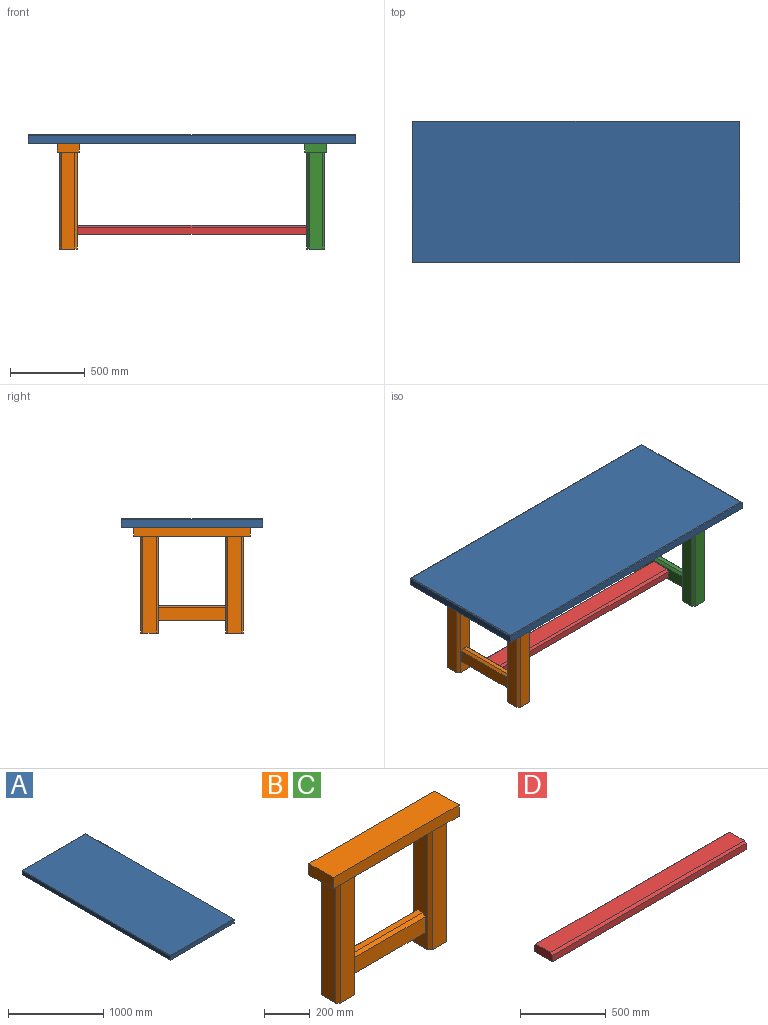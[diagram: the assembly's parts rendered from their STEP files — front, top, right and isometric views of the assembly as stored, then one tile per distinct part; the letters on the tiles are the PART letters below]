
ASSEMBLY  parts=4 mates=4
PART A: 10 faces, bbox 950x2200x55 mm
  f0: plane 950x50mm, normal (0,1,0), area 47500mm2, adj f1,f3,f4,f6
  f1: plane 2200x50mm, normal (-1,0,0), area 110000mm2, adj f0,f2,f4,f7
  f2: plane 950x50mm, normal (0,-1,0), area 47500mm2, adj f1,f3,f4,f9
  f3: plane 2200x50mm, normal (1,0,0), area 110000mm2, adj f0,f2,f4,f8
  f4: plane 2200x950mm, normal (0,0,-1), area 2090000mm2, adj f0,f1,f2,f3
  f5: plane 2190x940mm, normal (0,0,1), area 2058600mm2, adj f6,f7,f8,f9
  f6: cylinder r=5mm len=950mm, axis (-1,0,0), area 7432.7mm2, adj f0,f5,f7,f8
  f7: cylinder r=5mm len=2200mm, axis (0,-1,0), area 17250.2mm2, adj f1,f5,f6,f9
  f8: cylinder r=5mm len=2200mm, axis (0,1,0), area 17250.2mm2, adj f3,f5,f6,f9
  f9: cylinder r=5mm len=950mm, axis (1,0,0), area 7432.7mm2, adj f2,f5,f7,f8
PART B: 30 faces, bbox 780x150x710 mm
  f0: plane 150x60mm, normal (-1,0,0), area 9000mm2, adj f1,f3,f4,f5
  f1: plane 780x60mm, normal (0,-1,0), area 46800mm2, adj f0,f2,f4,f5
  f2: plane 150x60mm, normal (1,0,0), area 9000mm2, adj f1,f3,f4,f5
  f3: plane 780x60mm, normal (0,1,0), area 46800mm2, adj f0,f2,f4,f5
  f4: plane 780x150mm, normal (0,0,1), area 117000mm2, adj f0,f1,f2,f3
  f5: plane 780x150mm, normal (0,0,-1), area 89100mm2, adj f0,f1,f2,f3,f6,f7,f8,f9
  f6: plane 650x90mm, normal (0,-1,0), area 58500mm2, adj f5,f10,f17,f22
  f7: plane 650x90mm, normal (-1,0,0), area 52725mm2, adj f5,f10,f22,f23,f24,f25,f26,f27
  f8: plane 650x90mm, normal (0,1,0), area 58500mm2, adj f5,f10,f16,f23
  f9: plane 650x90mm, normal (1,0,0), area 58500mm2, adj f5,f10,f16,f17
  f10: plane 120x120mm, normal (0,0,-1), area 13950mm2, adj f6,f7,f8,f9,f16,f17,f22,f23
  f11: plane 650x90mm, normal (0,-1,0), area 58500mm2, adj f5,f15,f18,f19
  f12: plane 650x90mm, normal (-1,0,0), area 58500mm2, adj f5,f15,f19,f20
  f13: plane 650x90mm, normal (0,1,0), area 58500mm2, adj f5,f15,f20,f21
  f14: plane 650x90mm, normal (1,0,0), area 52725mm2, adj f5,f15,f18,f21,f24,f25,f26,f27
  f15: plane 120x120mm, normal (0,0,-1), area 13950mm2, adj f11,f12,f13,f14,f18,f19,f20,f21
  f16: plane 650x15mm, normal (0.71,0.71,0), area 13788.6mm2, adj f5,f8,f9,f10
  f17: plane 650x15mm, normal (0.71,-0.71,0), area 13788.6mm2, adj f5,f6,f9,f10
  f18: plane 650x15mm, normal (0.71,-0.71,0), area 13788.6mm2, adj f5,f11,f14,f15
  f19: plane 650x15mm, normal (-0.71,-0.71,0), area 13788.6mm2, adj f5,f11,f12,f15
  f20: plane 650x15mm, normal (-0.71,0.71,0), area 13788.6mm2, adj f5,f12,f13,f15
  f21: plane 650x15mm, normal (0.71,0.71,0), area 13788.6mm2, adj f5,f13,f14,f15
  f22: plane 650x15mm, normal (-0.71,-0.71,0), area 13788.6mm2, adj f5,f6,f7,f10
  f23: plane 650x15mm, normal (-0.71,0.71,0), area 13788.6mm2, adj f5,f7,f8,f10
  f24: plane 450x30mm, normal (0,0,1), area 13500mm2, adj f7,f14,f28,f29
  f25: plane 450x85mm, normal (0,1,0), area 38250mm2, adj f7,f14,f26,f29
  f26: plane 450x60mm, normal (0,0,-1), area 27000mm2, adj f7,f14,f25,f27
  f27: plane 450x85mm, normal (0,-1,0), area 38250mm2, adj f7,f14,f26,f28
  f28: plane 450x15mm, normal (0,-0.71,0.71), area 9545.9mm2, adj f7,f14,f24,f27
  f29: plane 450x15mm, normal (0,0.71,0.71), area 9545.9mm2, adj f7,f14,f24,f25
PART C: same geometry as B
PART D: 8 faces, bbox 1600x150x60 mm
  f0: plane 150x60mm, normal (-1,0,0), area 8775mm2, adj f1,f3,f4,f5,f6,f7
  f1: plane 1600x45mm, normal (0,-1,0), area 72000mm2, adj f0,f2,f5,f7
  f2: plane 150x60mm, normal (1,0,0), area 8775mm2, adj f1,f3,f4,f5,f6,f7
  f3: plane 1600x45mm, normal (0,1,0), area 72000mm2, adj f0,f2,f5,f6
  f4: plane 1600x120mm, normal (0,0,1), area 192000mm2, adj f0,f2,f6,f7
  f5: plane 1600x150mm, normal (0,0,-1), area 240000mm2, adj f0,f1,f2,f3
  f6: plane 1600x15mm, normal (0,0.71,0.71), area 33941.1mm2, adj f0,f2,f3,f4
  f7: plane 1600x15mm, normal (0,-0.71,0.71), area 33941.1mm2, adj f0,f1,f2,f4
PLACE A rot(axis=(0,0,1),90deg) t=(2877.51,-730.43,-245.15)mm
PLACE B rot(axis=(0,0,-1),90deg) t=(1337.73,-427.15,-360.15)mm
PLACE C rot(axis=(0,0,1),90deg) t=(2998.17,-882.13,-360.15)mm
PLACE D rot(axis=(0,0,-1),180deg) t=(2830.17,-665.32,-912.01)mm
MATE parallel A.f2 <-> C.f1  axis (1,0,0) through (3267.95,-654.64,-275.15)mm
MATE fastened B.f25 <-> D.f2  axis (1,0,0) through (1367.95,-654.64,-882.65)mm
MATE fastened C.f25 <-> D.f0  axis (-1,0,0) through (2967.95,-654.64,-882.65)mm
MATE planar A.f4 <-> B.f4  axis (0,0,-1) through (2167.95,-654.64,-300.15)mm
